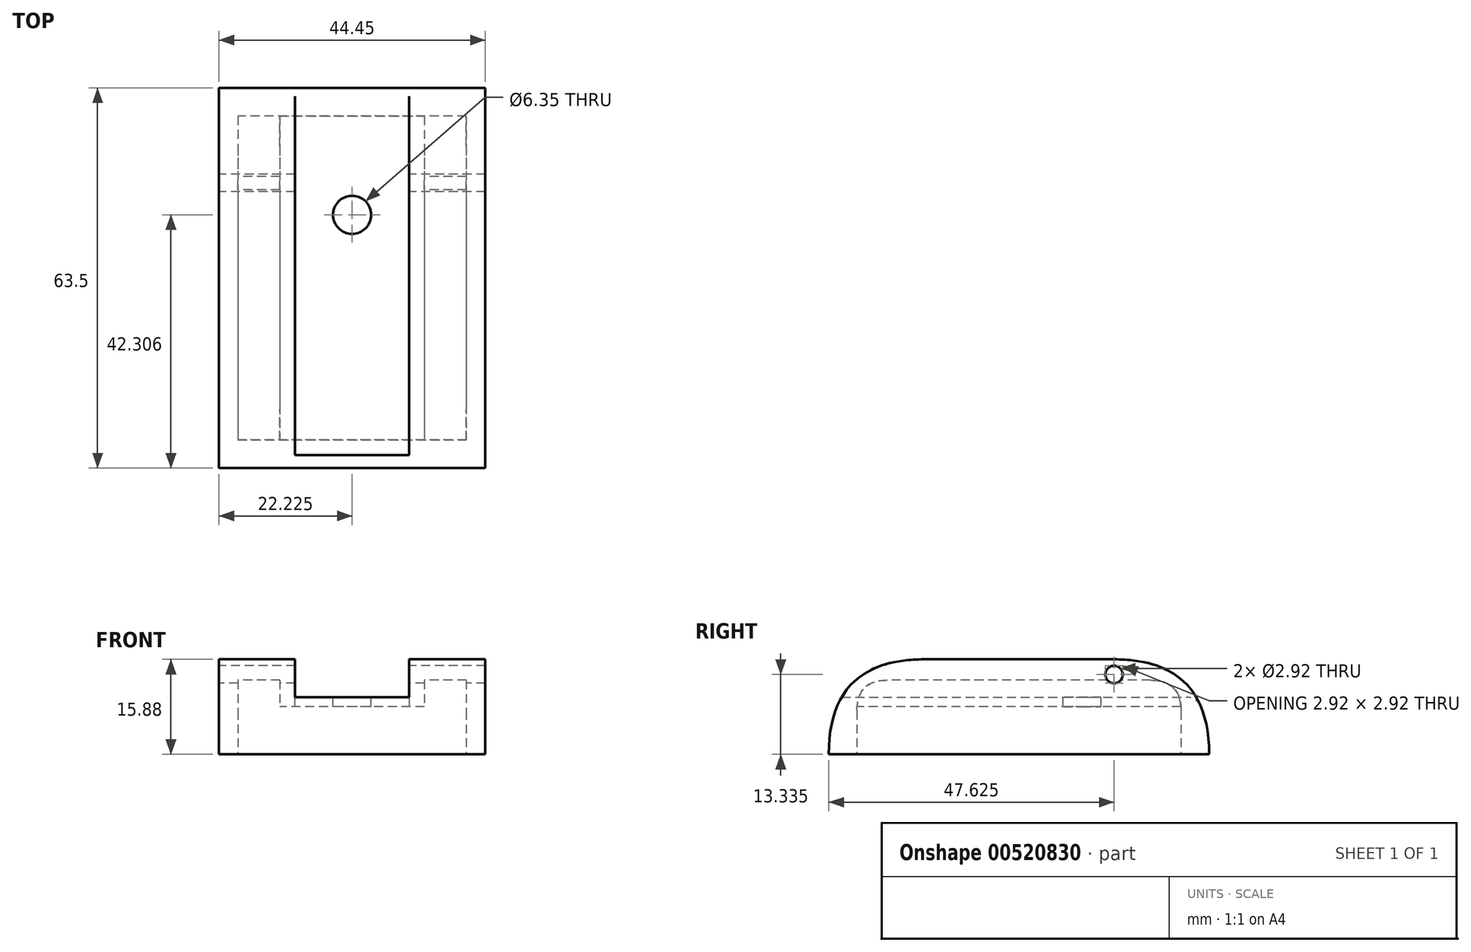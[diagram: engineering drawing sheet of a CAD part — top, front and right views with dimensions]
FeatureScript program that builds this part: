
annotation { "Feature Type Name" : "Feature", "Feature Type Description" : "" }
export const myFeature = defineFeature(function(context is Context, id is Id, definition is map)
    precondition{}
    {
        {
            var Q0;
            Q0=qCreatedBy(makeId("Top.planeOp"),FACE);
            var sketch = newSketch(context, id + "F0", { "sketchPlane" : qUnion([Q0])});
            skLineSegment(sketch, "E0.bottom", {"start": v(0, 0) * mm, "end": v(-44.45, 0) * mm});
            skLineSegment(sketch, "E0.top", {"start": v(0, 63.5) * mm, "end": v(-44.45, 63.5) * mm});
            skLineSegment(sketch, "E0.left", {"start": v(0, 0) * mm, "end": v(0, 63.5) * mm});
            skLineSegment(sketch, "E0.right", {"start": v(-44.45, 0) * mm, "end": v(-44.45, 63.5) * mm});
            skSolve(sketch);
        }
        {
            var Q0;
            Q0=makeQuery(id+"F0.imprint","IMPRINT",FACE,{"disambiguationData":[TD([[makeQuery(id+"F0.imprint","IMPRINT",EDGE,{"derivedFrom":sQuery(id+"F0.wireOp",EDGE,"E0.bottom")}),-1.0]])]});
            extrude(context, id + "F1", {"entities" : qUnion([Q0]), "depth" : 15.88 * mm, "offsetDistance" : 25.4 * mm});
        }
        {
            var Q0;
            Q0=makeQuery(id+"F1.opExtrude","CAP_FACE",FACE,{"disambiguationData":[OSD([sQuery(id+"F0.wireOp",EDGE,"E0.bottom"),sQuery(id+"F0.wireOp",EDGE,"E0.top"),sQuery(id+"F0.wireOp",EDGE,"E0.left"),sQuery(id+"F0.wireOp",EDGE,"E0.right")])],"isStart":false});
            var sketch = newSketch(context, id + "F2", { "sketchPlane" : qUnion([Q0])});
            skLineSegment(sketch, "E1.bottom", {"start": v(0, 0) * mm, "end": v(-12.7, 0) * mm});
            skLineSegment(sketch, "E1.top", {"start": v(0, 63.5) * mm, "end": v(-12.7, 63.5) * mm});
            skLineSegment(sketch, "E1.left", {"start": v(0, 0) * mm, "end": v(0, 63.5) * mm});
            skLineSegment(sketch, "E1.right", {"start": v(-12.7, 0) * mm, "end": v(-12.7, 63.5) * mm});
            skLineSegment(sketch, "E2.bottom", {"start": v(-44.45, 0) * mm, "end": v(-31.75, 0) * mm});
            skLineSegment(sketch, "E2.top", {"start": v(-44.45, 63.5) * mm, "end": v(-31.75, 63.5) * mm});
            skLineSegment(sketch, "E2.left", {"start": v(-44.45, 0) * mm, "end": v(-44.45, 63.5) * mm});
            skLineSegment(sketch, "E2.right", {"start": v(-31.75, 0) * mm, "end": v(-31.75, 63.5) * mm});
            skSolve(sketch);
        }
        {
            var Q0;
            {var subQ0=sQuery(id+"F2.wireOp",EDGE,"E1.right");Q0=makeQuery(id+"F2.imprint","IMPRINT",FACE,{"disambiguationData":[TD([[makeQuery(id+"F2.imprint","IMPRINT",EDGE,{"derivedFrom":subQ0}),1.0]])]});}
            extrude(context, id + "F3", {"entities" : qUnion([Q0]), "operationType" : NewBodyOperationType.REMOVE, "oppositeDirection" : true, "depth" : 6.35 * mm, "offsetDistance" : 25.4 * mm});
        }
        {
            var Q0;
            {var subQ0=sQuery(id+"F0.wireOp",EDGE,"E0.left");var subQ1=sQuery(id+"F0.wireOp",EDGE,"E0.top");Q0=makeQuery(id+"F3.boolean.opBoolean","SPLIT",EDGE,{"disambiguationData":[TD([makeQuery(id+"F1.opExtrude","SWEPT_FACE",FACE,{"disambiguationData":[OSD([subQ0])]})])],"derivedFrom":makeQuery(id+"F1.opExtrude","CAP_EDGE",EDGE,{"disambiguationData":[OSD([subQ1])],"isStart":false})});}
            var Q1;
            {var subQ0=sQuery(id+"F0.wireOp",EDGE,"E0.right");var subQ1=sQuery(id+"F0.wireOp",EDGE,"E0.top");Q1=makeQuery(id+"F3.boolean.opBoolean","SPLIT",EDGE,{"disambiguationData":[TD([makeQuery(id+"F1.opExtrude","SWEPT_FACE",FACE,{"disambiguationData":[OSD([subQ0])]})])],"derivedFrom":makeQuery(id+"F1.opExtrude","CAP_EDGE",EDGE,{"disambiguationData":[OSD([subQ1])],"isStart":false})});}
            var Q2;
            {var subQ0=sQuery(id+"F0.wireOp",EDGE,"E0.bottom");var subQ1=sQuery(id+"F0.wireOp",EDGE,"E0.left");Q2=makeQuery(id+"F3.boolean.opBoolean","SPLIT",EDGE,{"disambiguationData":[TD([makeQuery(id+"F1.opExtrude","SWEPT_FACE",FACE,{"disambiguationData":[OSD([subQ1])]})])],"derivedFrom":makeQuery(id+"F1.opExtrude","CAP_EDGE",EDGE,{"disambiguationData":[OSD([subQ0])],"isStart":false})});}
            var Q3;
            {var subQ0=sQuery(id+"F0.wireOp",EDGE,"E0.bottom");var subQ1=sQuery(id+"F0.wireOp",EDGE,"E0.right");Q3=makeQuery(id+"F3.boolean.opBoolean","SPLIT",EDGE,{"disambiguationData":[TD([makeQuery(id+"F1.opExtrude","SWEPT_FACE",FACE,{"disambiguationData":[OSD([subQ1])]})])],"derivedFrom":makeQuery(id+"F1.opExtrude","CAP_EDGE",EDGE,{"disambiguationData":[OSD([subQ0])],"isStart":false})});}
            fillet(context, id + "F4", {"entities" : qUnion([Q0, Q1, Q2, Q3]), "radius" : 15.88 * mm, "tangentPropagation" : true, "rho" : 0.5, "crossSection" : FilletCrossSection.CONIC, "allowEdgeOverflow" : false});
        }
        {
            var Q0;
            Q0=makeQuery(id+"F3.boolean.opBoolean","COPY",FACE,{"derivedFrom":makeQuery(id+"F3.opExtrude","CAP_FACE",FACE,{"disambiguationData":[OSD([sQuery(id+"F0.wireOp",EDGE,"E0.bottom"),sQuery(id+"F0.wireOp",EDGE,"E0.top"),sQuery(id+"F2.wireOp",EDGE,"E1.right"),sQuery(id+"F2.wireOp",EDGE,"E2.right")])],"isStart":false})});
            var sketch = newSketch(context, id + "F5", { "sketchPlane" : qUnion([Q0])});
            skLineSegment(sketch, "E3", {"start": v(-12.7, 61.36) * mm, "end": v(-12.7, 42.3) * mm});
            skLineSegment(sketch, "E4", {"start": v(-12.7, 42.3) * mm, "end": v(-22.23, 42.3) * mm});
            skLineSegment(sketch, "E5", {"start": v(-22.23, 42.3) * mm, "end": v(-31.75, 42.3) * mm});
            skCircle(sketch, "E6", {"center": v(-22.23, 42.3) * mm, "radius": 3.18 * mm});
            skSolve(sketch);
        }
        {
            var Q0;
            {var subQ0=sQuery(id+"F5.wireOp",EDGE,"E5");var subQ1=sQuery(id+"F5.wireOp",EDGE,"E4");var subQ2=makeQuery(id+"F5.imprint","INTERSECT",VERTEX,{"derivedFrom":[subQ1,subQ0]});Q0=makeQuery(id+"F5.imprint","IMPRINT",FACE,{"disambiguationData":[TD([[makeQuery(id+"F5.imprint","IMPRINT",EDGE,{"disambiguationData":[TD([[subQ2,1.0]])],"derivedFrom":subQ1}),1.0]])]});}
            var Q1;
            {var subQ0=sQuery(id+"F5.wireOp",EDGE,"E5");var subQ1=sQuery(id+"F5.wireOp",EDGE,"E4");var subQ2=makeQuery(id+"F5.imprint","INTERSECT",VERTEX,{"derivedFrom":[subQ1,subQ0]});Q1=makeQuery(id+"F5.imprint","IMPRINT",FACE,{"disambiguationData":[TD([[makeQuery(id+"F5.imprint","IMPRINT",EDGE,{"disambiguationData":[TD([[subQ2,1.0]])],"derivedFrom":subQ1}),-1.0]])]});}
            extrude(context, id + "F6", {"entities" : qUnion([Q0, Q1]), "operationType" : NewBodyOperationType.REMOVE, "oppositeDirection" : true, "depth" : 25.4 * mm, "offsetDistance" : 25.4 * mm});
        }
        {
            var Q0;
            Q0=makeQuery(id+"F1.opExtrude","CAP_FACE",FACE,{"disambiguationData":[OSD([sQuery(id+"F0.wireOp",EDGE,"E0.bottom"),sQuery(id+"F0.wireOp",EDGE,"E0.top"),sQuery(id+"F0.wireOp",EDGE,"E0.left"),sQuery(id+"F0.wireOp",EDGE,"E0.right")])],"isStart":true});
            var sketch = newSketch(context, id + "F7", { "sketchPlane" : qUnion([Q0])});
            skLineSegment(sketch, "E7", {"start": v(-44.45, 0) * mm, "end": v(-44.45, -4.7) * mm});
            skLineSegment(sketch, "E8", {"start": v(-44.45, -4.7) * mm, "end": v(-41.28, -4.7) * mm});
            skLineSegment(sketch, "E9", {"start": v(0, -63.5) * mm, "end": v(0, -58.8) * mm});
            skLineSegment(sketch, "E10", {"start": v(0, -58.8) * mm, "end": v(-3.17, -58.8) * mm});
            skLineSegment(sketch, "E11.bottom", {"start": v(-3.17, -58.8) * mm, "end": v(-41.27, -58.8) * mm});
            skLineSegment(sketch, "E11.top", {"start": v(-3.18, -4.7) * mm, "end": v(-41.28, -4.7) * mm});
            skLineSegment(sketch, "E11.left", {"start": v(-3.17, -58.8) * mm, "end": v(-3.18, -4.7) * mm});
            skLineSegment(sketch, "E11.right", {"start": v(-41.27, -58.8) * mm, "end": v(-41.27, -4.7) * mm});
            skSolve(sketch);
        }
        {
            var Q0;
            Q0=makeQuery(id+"F7.imprint","IMPRINT",FACE,{"disambiguationData":[TD([[makeQuery(id+"F7.imprint","IMPRINT",EDGE,{"derivedFrom":sQuery(id+"F7.wireOp",EDGE,"E11.bottom")}),-1.0]])]});
            extrude(context, id + "F8", {"entities" : qUnion([Q0]), "operationType" : NewBodyOperationType.REMOVE, "oppositeDirection" : true, "depth" : 7.94 * mm, "offsetDistance" : 25.4 * mm});
        }
        {
            var Q0;
            Q0=makeQuery(id+"F8.boolean.opBoolean","COPY",FACE,{"derivedFrom":makeQuery(id+"F8.opExtrude","CAP_FACE",FACE,{"disambiguationData":[OSD([sQuery(id+"F0.wireOp",EDGE,"E0.bottom"),sQuery(id+"F0.wireOp",EDGE,"E0.top"),sQuery(id+"F0.wireOp",EDGE,"E0.left"),sQuery(id+"F0.wireOp",EDGE,"E0.right"),sQuery(id+"F5.wireOp",EDGE,"E6"),sQuery(id+"F7.wireOp",EDGE,"E11.bottom"),sQuery(id+"F7.wireOp",EDGE,"E11.top"),sQuery(id+"F7.wireOp",EDGE,"E11.left"),sQuery(id+"F7.wireOp",EDGE,"E11.right")])],"isStart":false})});
            var sketch = newSketch(context, id + "F9", { "sketchPlane" : qUnion([Q0])});
            skLineSegment(sketch, "E12.bottom", {"start": v(-41.27, -58.8) * mm, "end": v(-34.29, -58.8) * mm});
            skLineSegment(sketch, "E12.top", {"start": v(-41.28, -4.7) * mm, "end": v(-34.29, -4.7) * mm});
            skLineSegment(sketch, "E12.left", {"start": v(-41.27, -58.8) * mm, "end": v(-41.28, -4.7) * mm});
            skLineSegment(sketch, "E12.right", {"start": v(-34.29, -58.8) * mm, "end": v(-34.29, -4.7) * mm});
            skLineSegment(sketch, "E13.bottom", {"start": v(-3.17, -58.8) * mm, "end": v(-10.16, -58.8) * mm});
            skLineSegment(sketch, "E13.top", {"start": v(-3.18, -4.7) * mm, "end": v(-10.16, -4.7) * mm});
            skLineSegment(sketch, "E13.left", {"start": v(-3.17, -58.8) * mm, "end": v(-3.18, -4.7) * mm});
            skLineSegment(sketch, "E13.right", {"start": v(-10.16, -58.8) * mm, "end": v(-10.16, -4.7) * mm});
            skSolve(sketch);
        }
        {
            var Q0;
            Q0=makeQuery(id+"F9.imprint","IMPRINT",FACE,{"disambiguationData":[TD([[makeQuery(id+"F9.imprint","IMPRINT",EDGE,{"derivedFrom":sQuery(id+"F9.wireOp",EDGE,"E12.bottom")}),-1.0]])]});
            var Q1;
            Q1=makeQuery(id+"F9.imprint","IMPRINT",FACE,{"disambiguationData":[TD([[makeQuery(id+"F9.imprint","IMPRINT",EDGE,{"derivedFrom":sQuery(id+"F9.wireOp",EDGE,"E13.bottom")}),-1.0]])]});
            extrude(context, id + "F10", {"entities" : qUnion([Q0, Q1]), "operationType" : NewBodyOperationType.REMOVE, "oppositeDirection" : true, "depth" : 4.44 * mm, "offsetDistance" : 25.4 * mm});
        }
        {
            var Q0;
            Q0=makeQuery(id+"F10.boolean.opBoolean","COPY",EDGE,{"derivedFrom":makeQuery(id+"F10.opExtrude","CAP_EDGE",EDGE,{"disambiguationData":[OSD([sQuery(id+"F9.wireOp",EDGE,"E12.top")])],"isStart":false})});
            var Q1;
            Q1=makeQuery(id+"F10.boolean.opBoolean","COPY",EDGE,{"derivedFrom":makeQuery(id+"F10.opExtrude","CAP_EDGE",EDGE,{"disambiguationData":[OSD([sQuery(id+"F9.wireOp",EDGE,"E12.bottom")])],"isStart":false})});
            fillet(context, id + "F11", {"entities" : qUnion([Q0, Q1]), "radius" : 5.08 * mm, "tangentPropagation" : true, "rho" : 0.5, "crossSection" : FilletCrossSection.CONIC, "allowEdgeOverflow" : false});
        }
        {
            var Q0;
            {var subQ0=sQuery(id+"F0.wireOp",EDGE,"E0.right");var subQ1=makeQuery(id+"F1.opExtrude","SWEPT_FACE",FACE,{"disambiguationData":[OSD([subQ0])]});var subQ2=sQuery(id+"F0.wireOp",EDGE,"E0.bottom");Q0=makeQuery(id+"F4.opFillet","BLEND_EDGE",EDGE,{"blendedFrom":[makeQuery(id+"F3.boolean.opBoolean","SPLIT",EDGE,{"disambiguationData":[TD([subQ1])],"derivedFrom":makeQuery(id+"F1.opExtrude","CAP_EDGE",EDGE,{"disambiguationData":[OSD([subQ2])],"isStart":false})}),subQ1],"blendedInto":[subQ1]});}
            var Q1;
            {var subQ0=makeQuery(id+"F3.opExtrude","SWEPT_FACE",FACE,{"disambiguationData":[OSD([sQuery(id+"F2.wireOp",EDGE,"E2.right")])]});var subQ1=sQuery(id+"F0.wireOp",EDGE,"E0.bottom");var subQ2=sQuery(id+"F0.wireOp",EDGE,"E0.right");Q1=makeQuery(id+"F4.opFillet","BLEND_EDGE",EDGE,{"blendedFrom":[makeQuery(id+"F3.boolean.opBoolean","SPLIT",EDGE,{"disambiguationData":[TD([makeQuery(id+"F1.opExtrude","SWEPT_FACE",FACE,{"disambiguationData":[OSD([subQ2])]})])],"derivedFrom":makeQuery(id+"F1.opExtrude","CAP_EDGE",EDGE,{"disambiguationData":[OSD([subQ1])],"isStart":false})}),makeQuery(id+"F3.boolean.opBoolean","COPY",FACE,{"derivedFrom":subQ0})],"blendedInto":[makeQuery(id+"F3.boolean.opBoolean","COPY",FACE,{"derivedFrom":subQ0})]});}
            var Q2;
            {var subQ0=sQuery(id+"F2.wireOp",EDGE,"E2.right");var subQ1=sQuery(id+"F0.wireOp",EDGE,"E0.top");var subQ2=sQuery(id+"F0.wireOp",EDGE,"E0.bottom");var subQ3=sQuery(id+"F0.wireOp",EDGE,"E0.right");Q2=makeQuery(id+"F4.opFillet","BLEND_EDGE",EDGE,{"blendedFrom":[makeQuery(id+"F3.boolean.opBoolean","SPLIT",EDGE,{"disambiguationData":[TD([makeQuery(id+"F1.opExtrude","SWEPT_FACE",FACE,{"disambiguationData":[OSD([subQ3])]})])],"derivedFrom":makeQuery(id+"F1.opExtrude","CAP_EDGE",EDGE,{"disambiguationData":[OSD([subQ2])],"isStart":false})}),makeQuery(id+"F3.boolean.opBoolean","COPY",FACE,{"derivedFrom":makeQuery(id+"F3.opExtrude","CAP_FACE",FACE,{"disambiguationData":[OSD([subQ2,subQ1,sQuery(id+"F2.wireOp",EDGE,"E1.right"),subQ0])],"isStart":false})})],"blendedInto":[makeQuery(id+"F3.boolean.opBoolean","COPY",FACE,{"derivedFrom":makeQuery(id+"F3.opExtrude","CAP_FACE",FACE,{"disambiguationData":[OSD([subQ2,subQ1,sQuery(id+"F2.wireOp",EDGE,"E1.right"),subQ0])],"isStart":false})})]});}
            var Q3;
            {var subQ0=sQuery(id+"F0.wireOp",EDGE,"E0.bottom");var subQ1=sQuery(id+"F0.wireOp",EDGE,"E0.right");Q3=makeQuery(id+"F4.opFillet","BLEND_EDGE",EDGE,{"blendedFrom":[makeQuery(id+"F3.boolean.opBoolean","SPLIT",EDGE,{"disambiguationData":[TD([makeQuery(id+"F1.opExtrude","SWEPT_FACE",FACE,{"disambiguationData":[OSD([subQ1])]})])],"derivedFrom":makeQuery(id+"F1.opExtrude","CAP_EDGE",EDGE,{"disambiguationData":[OSD([subQ0])],"isStart":false})}),makeQuery(id+"F3.boolean.opBoolean","COPY",FACE,{"derivedFrom":makeQuery(id+"F3.opExtrude","SWEPT_FACE",FACE,{"disambiguationData":[OSD([sQuery(id+"F2.wireOp",EDGE,"E1.right")])]})})],"blendedInto":[makeQuery(id+"F3.boolean.opBoolean","COPY",FACE,{"derivedFrom":makeQuery(id+"F3.opExtrude","SWEPT_FACE",FACE,{"disambiguationData":[OSD([sQuery(id+"F2.wireOp",EDGE,"E1.right")])]})})]});}
            var Q4;
            {var subQ0=sQuery(id+"F0.wireOp",EDGE,"E0.left");var subQ1=sQuery(id+"F0.wireOp",EDGE,"E0.bottom");var subQ2=sQuery(id+"F0.wireOp",EDGE,"E0.right");Q4=makeQuery(id+"F4.opFillet","BLEND_EDGE",EDGE,{"blendedFrom":[makeQuery(id+"F3.boolean.opBoolean","SPLIT",EDGE,{"disambiguationData":[TD([makeQuery(id+"F1.opExtrude","SWEPT_FACE",FACE,{"disambiguationData":[OSD([subQ2])]})])],"derivedFrom":makeQuery(id+"F1.opExtrude","CAP_EDGE",EDGE,{"disambiguationData":[OSD([subQ1])],"isStart":false})}),makeQuery(id+"F1.opExtrude","SWEPT_FACE",FACE,{"disambiguationData":[OSD([subQ0])]})],"blendedInto":[makeQuery(id+"F1.opExtrude","SWEPT_FACE",FACE,{"disambiguationData":[OSD([subQ0])]})]});}
            var Q5;
            Q5=makeQuery(id+"F8.boolean.opBoolean","COPY",EDGE,{"derivedFrom":makeQuery(id+"F8.opExtrude","CAP_EDGE",EDGE,{"disambiguationData":[OSD([sQuery(id+"F7.wireOp",EDGE,"E11.top")])],"isStart":true})});
            var Q6;
            Q6=makeQuery(id+"F8.boolean.opBoolean","COPY",EDGE,{"derivedFrom":makeQuery(id+"F8.opExtrude","CAP_EDGE",EDGE,{"disambiguationData":[OSD([sQuery(id+"F7.wireOp",EDGE,"E11.bottom")])],"isStart":true})});
            var Q7;
            {var subQ0=sQuery(id+"F2.wireOp",EDGE,"E1.right");var subQ1=sQuery(id+"F0.wireOp",EDGE,"E0.top");var subQ2=sQuery(id+"F0.wireOp",EDGE,"E0.bottom");var subQ3=sQuery(id+"F0.wireOp",EDGE,"E0.left");Q7=makeQuery(id+"F4.opFillet","BLEND_EDGE",EDGE,{"blendedFrom":[makeQuery(id+"F3.boolean.opBoolean","SPLIT",EDGE,{"disambiguationData":[TD([makeQuery(id+"F1.opExtrude","SWEPT_FACE",FACE,{"disambiguationData":[OSD([subQ3])]})])],"derivedFrom":makeQuery(id+"F1.opExtrude","CAP_EDGE",EDGE,{"disambiguationData":[OSD([subQ1])],"isStart":false})}),makeQuery(id+"F3.boolean.opBoolean","COPY",FACE,{"derivedFrom":makeQuery(id+"F3.opExtrude","CAP_FACE",FACE,{"disambiguationData":[OSD([subQ2,subQ1,subQ0,sQuery(id+"F2.wireOp",EDGE,"E2.right")])],"isStart":false})})],"blendedInto":[makeQuery(id+"F3.boolean.opBoolean","COPY",FACE,{"derivedFrom":makeQuery(id+"F3.opExtrude","CAP_FACE",FACE,{"disambiguationData":[OSD([subQ2,subQ1,subQ0,sQuery(id+"F2.wireOp",EDGE,"E2.right")])],"isStart":false})})]});}
            fillet(context, id + "F12", {"entities" : qUnion([Q0, Q1, Q2, Q3, Q4, Q5, Q6, Q7]), "radius" : 2.54 * mm, "tangentPropagation" : true, "allowEdgeOverflow" : false});
        }
        {
            var Q0;
            Q0=makeQuery(id+"F1.opExtrude","SWEPT_FACE",FACE,{"disambiguationData":[OSD([sQuery(id+"F0.wireOp",EDGE,"E0.right")])]});
            var sketch = newSketch(context, id + "F13", { "sketchPlane" : qUnion([Q0])});
            skCircle(sketch, "E14", {"center": v(-47.63, 13.33) * mm, "radius": 1.46 * mm});
            skSolve(sketch);
        }
        {
            var Q0;
            {var subQ0=sQuery(id+"F13.wireOp",EDGE,"E14");var subQ1=sQuery(id+"F0.wireOp",EDGE,"E0.right");var subQ2=makeQuery(id+"F1.opExtrude","SWEPT_FACE",FACE,{"disambiguationData":[OSD([subQ1])]});var subQ3=subQ2;var subQ4=makeQuery(id+"F12.opFillet","BLEND_EDGE",EDGE,{"blendedFrom":[makeQuery(id+"F1.opExtrude","CAP_EDGE",EDGE,{"disambiguationData":[OSD([subQ1])],"isStart":false}),subQ3],"blendedInto":[subQ3]});var subQ5=makeQuery(id+"F13.imprint","INTERSECT",VERTEX,{"derivedFrom":[subQ4,subQ0]});Q0=makeQuery(id+"F13.imprint","IMPRINT",FACE,{"disambiguationData":[TD([[makeQuery(id+"F13.imprint","IMPRINT",EDGE,{"disambiguationData":[TD([[subQ5,1.0]])],"derivedFrom":subQ0}),1.0]])]});}
            var Q1;
            {var subQ0=sQuery(id+"F13.wireOp",EDGE,"E14");var subQ1=sQuery(id+"F0.wireOp",EDGE,"E0.right");var subQ2=makeQuery(id+"F1.opExtrude","SWEPT_FACE",FACE,{"disambiguationData":[OSD([subQ1])]});var subQ3=subQ2;var subQ4=makeQuery(id+"F12.opFillet","BLEND_EDGE",EDGE,{"blendedFrom":[makeQuery(id+"F1.opExtrude","CAP_EDGE",EDGE,{"disambiguationData":[OSD([subQ1])],"isStart":false}),subQ3],"blendedInto":[subQ3]});var subQ5=makeQuery(id+"F13.imprint","INTERSECT",VERTEX,{"derivedFrom":[subQ4,subQ0]});Q1=makeQuery(id+"F13.imprint","IMPRINT",FACE,{"disambiguationData":[TD([[makeQuery(id+"F13.imprint","IMPRINT",EDGE,{"disambiguationData":[TD([[subQ5,-1.0]])],"derivedFrom":subQ0}),1.0]])]});}
            extrude(context, id + "F14", {"entities" : qUnion([Q0, Q1]), "operationType" : NewBodyOperationType.REMOVE, "oppositeDirection" : true, "depth" : 76.2 * mm, "offsetDistance" : 25.4 * mm});
        }
    });
